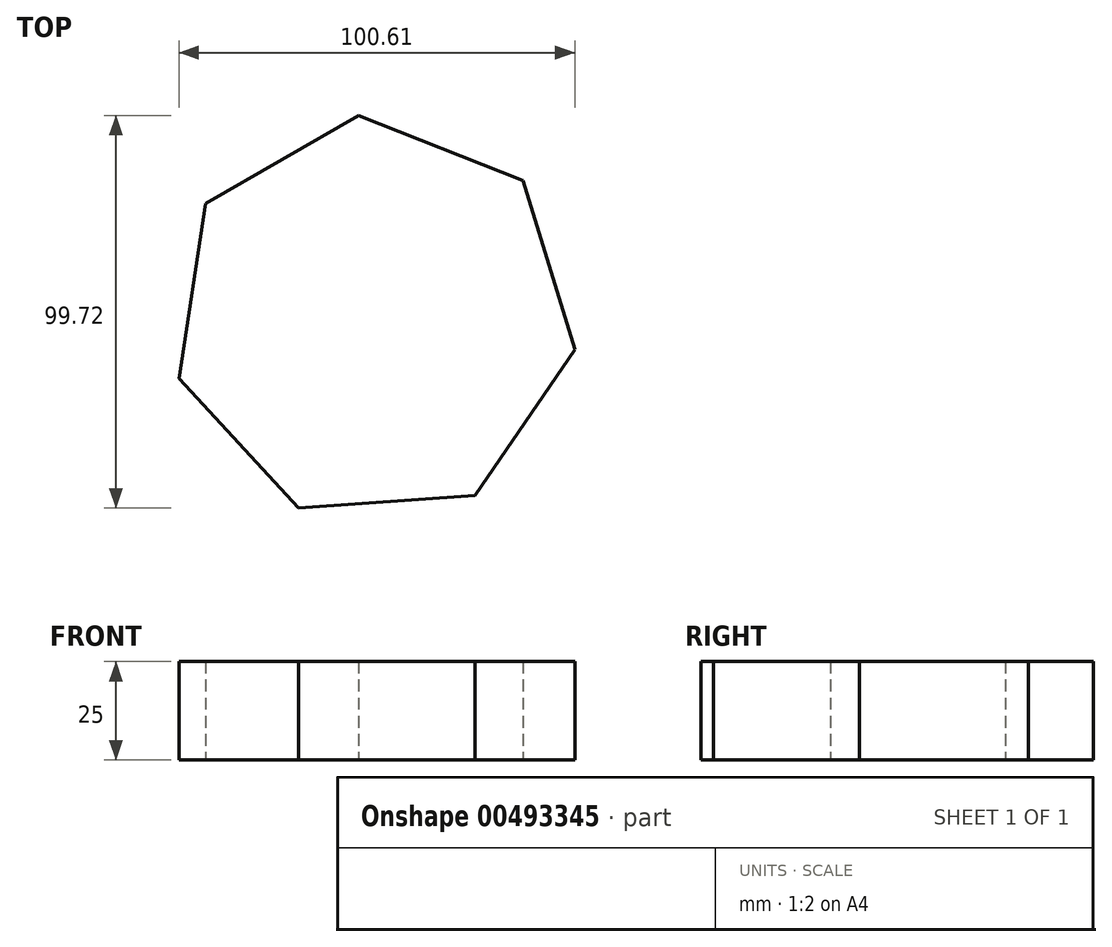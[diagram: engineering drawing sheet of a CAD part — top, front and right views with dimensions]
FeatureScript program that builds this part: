
annotation { "Feature Type Name" : "Feature", "Feature Type Description" : "" }
export const myFeature = defineFeature(function(context is Context, id is Id, definition is map)
    precondition{}
    {
        {
            var Q0;
            Q0=qCreatedBy(makeId("Top.planeOp"),FACE);
            var sketch = newSketch(context, id + "F0", { "sketchPlane" : qUnion([Q0])});
            skCircle(sketch, "E0.cCircle", {"center": v(0, 0) * mm, "radius": 51.74 * mm, "construction": true});
            skLineSegment(sketch, "E0.0", {"start": v(-42.69, 29.24) * mm, "end": v(-3.76, 51.6) * mm});
            skLineSegment(sketch, "E0.1", {"start": v(-3.76, 51.6) * mm, "end": v(38, 35.11) * mm});
            skLineSegment(sketch, "E0.2", {"start": v(38, 35.11) * mm, "end": v(51.14, -7.82) * mm});
            skLineSegment(sketch, "E0.3", {"start": v(51.14, -7.82) * mm, "end": v(25.77, -44.86) * mm});
            skLineSegment(sketch, "E0.4", {"start": v(25.77, -44.86) * mm, "end": v(-19, -48.12) * mm});
            skLineSegment(sketch, "E0.5", {"start": v(-19, -48.12) * mm, "end": v(-49.47, -15.14) * mm});
            skLineSegment(sketch, "E0.6", {"start": v(-49.47, -15.14) * mm, "end": v(-42.69, 29.24) * mm});
            skSolve(sketch);
        }
        {
            var Q0;
            Q0=makeQuery(id+"F0.imprint","IMPRINT",FACE,{"disambiguationData":[TD([[makeQuery(id+"F0.imprint","IMPRINT",EDGE,{"derivedFrom":sQuery(id+"F0.wireOp",EDGE,"E0.0")}),-1.0]])]});
            extrude(context, id + "F1", {"entities" : qUnion([Q0]), "depth" : 25 * mm});
        }
    });
